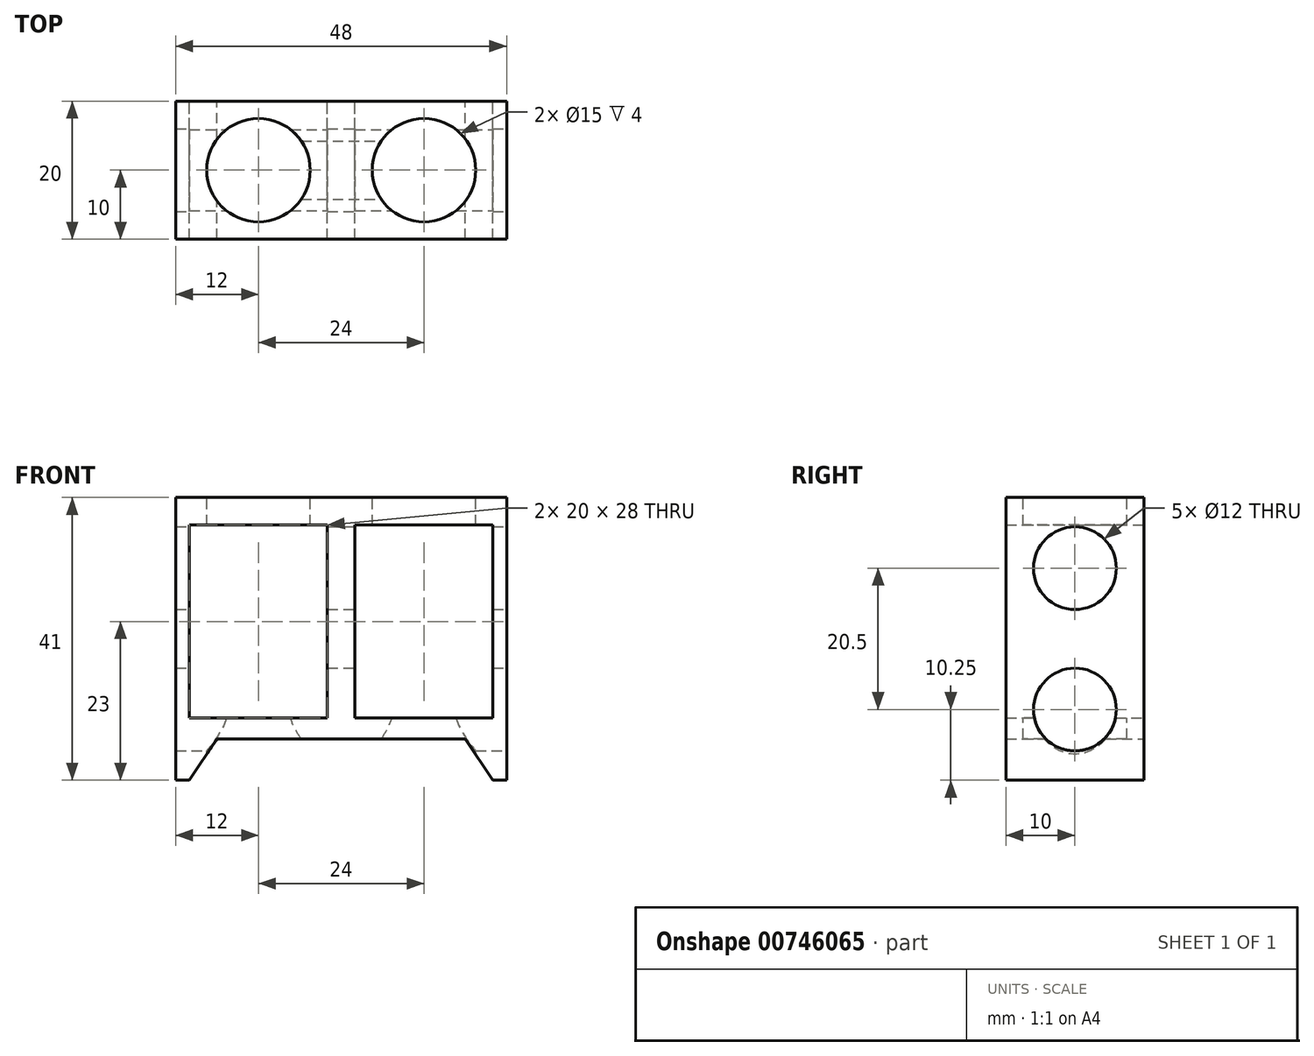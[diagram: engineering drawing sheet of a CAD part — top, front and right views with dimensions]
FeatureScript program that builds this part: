
annotation { "Feature Type Name" : "Feature", "Feature Type Description" : "" }
export const myFeature = defineFeature(function(context is Context, id is Id, definition is map)
    precondition{}
    {
        {
            var Q0;
            Q0=qCreatedBy(makeId("Front.planeOp"),FACE);
            var sketch = newSketch(context, id + "F0", { "sketchPlane" : qUnion([Q0])});
            skLineSegment(sketch, "E0", {"start": v(0, 0) * mm, "end": v(0, 45.25) * mm});
            skLineSegment(sketch, "E1", {"start": v(0, 0) * mm, "end": v(18, 0) * mm});
            skLineSegment(sketch, "E2", {"start": v(22, -6) * mm, "end": v(18, 0) * mm});
            skLineSegment(sketch, "E3", {"start": v(22, 35) * mm, "end": v(0, 35) * mm});
            skLineSegment(sketch, "E4", {"start": v(22, -6) * mm, "end": v(24, -6) * mm});
            skLineSegment(sketch, "E5", {"start": v(24, -6) * mm, "end": v(24, 35) * mm});
            skLineSegment(sketch, "E6", {"start": v(24, 35) * mm, "end": v(22, 35) * mm});
            skLineSegment(sketch, "E7", {"start": v(0, 0) * mm, "end": v(0, 3) * mm});
            skLineSegment(sketch, "E8", {"start": v(0, 3) * mm, "end": v(22, 3) * mm});
            skLineSegment(sketch, "E9", {"start": v(0, 3) * mm, "end": v(2, 3) * mm});
            skLineSegment(sketch, "E10", {"start": v(2, 3) * mm, "end": v(2, 31) * mm});
            skLineSegment(sketch, "E11", {"start": v(2, 31) * mm, "end": v(22, 31) * mm});
            skLineSegment(sketch, "E12", {"start": v(22, 31) * mm, "end": v(22, 3) * mm});
            skLineSegment(sketch, "E13.MirrorCS", {"start": v(-22, 35) * mm, "end": v(0, 35) * mm});
            skLineSegment(sketch, "E14.MirrorCS", {"start": v(-24, 35) * mm, "end": v(-22, 35) * mm});
            skLineSegment(sketch, "E15.MirrorCS", {"start": v(-24, -6) * mm, "end": v(-24, 35) * mm});
            skLineSegment(sketch, "E16.MirrorCS", {"start": v(-22, -6) * mm, "end": v(-18, 0) * mm});
            skLineSegment(sketch, "E17.MirrorCS", {"start": v(0, 0) * mm, "end": v(-18, 0) * mm});
            skLineSegment(sketch, "E18.MirrorCS", {"start": v(-22, -6) * mm, "end": v(-24, -6) * mm});
            skLineSegment(sketch, "E19.MirrorCS", {"start": v(0, 3) * mm, "end": v(-22, 3) * mm});
            skLineSegment(sketch, "E20.MirrorCS", {"start": v(-2, 3) * mm, "end": v(-2, 31) * mm});
            skLineSegment(sketch, "E21.MirrorCS", {"start": v(-22, 31) * mm, "end": v(-22, 3) * mm});
            skLineSegment(sketch, "E22.MirrorCS", {"start": v(-2, 31) * mm, "end": v(-22, 31) * mm});
            skSolve(sketch);
        }
        {
            var Q0;
            {var subQ6=sQuery(id+"F0.wireOp",EDGE,"E1");Q0=makeQuery(id+"F0.imprint","IMPRINT",FACE,{"disambiguationData":[TD([[makeQuery(id+"F0.imprint","IMPRINT",EDGE,{"derivedFrom":subQ6}),1.0]])]});}
            var Q1;
            {var subQ6=sQuery(id+"F0.wireOp",EDGE,"E13.MirrorCS");Q1=makeQuery(id+"F0.imprint","IMPRINT",FACE,{"disambiguationData":[TD([[makeQuery(id+"F0.imprint","IMPRINT",EDGE,{"derivedFrom":subQ6}),-1.0]])]});}
            extrude(context, id + "F1", {"entities" : qUnion([Q0, Q1]), "depth" : 20 * mm, "offsetDistance" : 25 * mm});
        }
        {
            var Q0;
            Q0=makeQuery(id+"F1.opExtrude","SWEPT_FACE",FACE,{"disambiguationData":[OSD([sQuery(id+"F0.wireOp",EDGE,"E3"),sQuery(id+"F0.wireOp",EDGE,"E6"),sQuery(id+"F0.wireOp",EDGE,"E13.MirrorCS"),sQuery(id+"F0.wireOp",EDGE,"E14.MirrorCS")])]});
            var sketch = newSketch(context, id + "F2", { "sketchPlane" : qUnion([Q0])});
            skLineSegment(sketch, "E23", {"start": v(-24, -10) * mm, "end": v(0, -10) * mm});
            skLineSegment(sketch, "E24", {"start": v(0, -10) * mm, "end": v(24, -10) * mm});
            skCircle(sketch, "E25", {"center": v(-12, -10) * mm, "radius": 7.5 * mm});
            skCircle(sketch, "E26", {"center": v(12, -10) * mm, "radius": 7.5 * mm});
            skSolve(sketch);
        }
        {
            var Q0;
            {var subQ0=sQuery(id+"F2.wireOp",EDGE,"E25");var subQ1=sQuery(id+"F2.wireOp",EDGE,"E23");var subQ2=makeQuery(id+"F2.imprint","INTERSECT",VERTEX,{"disambiguationData":[OD(0.0)],"derivedFrom":[subQ1,subQ0]});Q0=makeQuery(id+"F2.imprint","IMPRINT",FACE,{"disambiguationData":[TD([[makeQuery(id+"F2.imprint","IMPRINT",EDGE,{"disambiguationData":[TD([[subQ2,-1.0]])],"derivedFrom":subQ1}),-1.0]])]});}
            var Q1;
            {var subQ0=sQuery(id+"F2.wireOp",EDGE,"E25");var subQ1=sQuery(id+"F2.wireOp",EDGE,"E23");var subQ2=makeQuery(id+"F2.imprint","INTERSECT",VERTEX,{"disambiguationData":[OD(0.0)],"derivedFrom":[subQ1,subQ0]});Q1=makeQuery(id+"F2.imprint","IMPRINT",FACE,{"disambiguationData":[TD([[makeQuery(id+"F2.imprint","IMPRINT",EDGE,{"disambiguationData":[TD([[subQ2,-1.0]])],"derivedFrom":subQ1}),1.0]])]});}
            var Q2;
            {var subQ0=sQuery(id+"F2.wireOp",EDGE,"E26");var subQ1=sQuery(id+"F2.wireOp",EDGE,"E24");var subQ2=makeQuery(id+"F2.imprint","INTERSECT",VERTEX,{"disambiguationData":[OD(0.0)],"derivedFrom":[subQ1,subQ0]});Q2=makeQuery(id+"F2.imprint","IMPRINT",FACE,{"disambiguationData":[TD([[makeQuery(id+"F2.imprint","IMPRINT",EDGE,{"disambiguationData":[TD([[subQ2,-1.0]])],"derivedFrom":subQ1}),-1.0]])]});}
            var Q3;
            {var subQ0=sQuery(id+"F2.wireOp",EDGE,"E26");var subQ1=sQuery(id+"F2.wireOp",EDGE,"E24");var subQ2=makeQuery(id+"F2.imprint","INTERSECT",VERTEX,{"disambiguationData":[OD(0.0)],"derivedFrom":[subQ1,subQ0]});Q3=makeQuery(id+"F2.imprint","IMPRINT",FACE,{"disambiguationData":[TD([[makeQuery(id+"F2.imprint","IMPRINT",EDGE,{"disambiguationData":[TD([[subQ2,-1.0]])],"derivedFrom":subQ1}),1.0]])]});}
            extrude(context, id + "F3", {"entities" : qUnion([Q0, Q1, Q2, Q3]), "operationType" : NewBodyOperationType.REMOVE, "oppositeDirection" : true, "depth" : 50 * mm, "offsetDistance" : 25 * mm});
        }
        {
            var Q0;
            Q0=makeQuery(id+"F1.opExtrude","SWEPT_FACE",FACE,{"disambiguationData":[OSD([sQuery(id+"F0.wireOp",EDGE,"E5")])]});
            var sketch = newSketch(context, id + "F4", { "sketchPlane" : qUnion([Q0])});
            skLineSegment(sketch, "E27.0.0", {"start": v(0, -6) * mm, "end": v(0, 35) * mm});
            skLineSegment(sketch, "E27.0.1", {"start": v(0, 35) * mm, "end": v(-20, 35) * mm});
            skLineSegment(sketch, "E27.0.2", {"start": v(-20, 35) * mm, "end": v(-20, -6) * mm});
            skLineSegment(sketch, "E27.0.3", {"start": v(-20, -6) * mm, "end": v(0, -6) * mm});
            skLineSegment(sketch, "E28", {"start": v(-20, 14.5) * mm, "end": v(0, 14.5) * mm});
            skLineSegment(sketch, "E29", {"start": v(-10, 35) * mm, "end": v(-10, 14.5) * mm});
            skLineSegment(sketch, "E30", {"start": v(-10, 14.5) * mm, "end": v(-10, -6) * mm});
            skCircle(sketch, "E31", {"center": v(-10, 24.75) * mm, "radius": 6 * mm});
            skCircle(sketch, "E32", {"center": v(-10, 4.25) * mm, "radius": 6 * mm});
            skSolve(sketch);
        }
        {
            var Q0;
            {var subQ0=sQuery(id+"F4.wireOp",EDGE,"E31");var subQ1=sQuery(id+"F4.wireOp",EDGE,"E29");var subQ2=makeQuery(id+"F4.imprint","INTERSECT",VERTEX,{"disambiguationData":[OD(0.0)],"derivedFrom":[subQ1,subQ0]});Q0=makeQuery(id+"F4.imprint","IMPRINT",FACE,{"disambiguationData":[TD([[makeQuery(id+"F4.imprint","IMPRINT",EDGE,{"disambiguationData":[TD([[subQ2,-1.0]])],"derivedFrom":subQ1}),-1.0]])]});}
            var Q1;
            {var subQ0=sQuery(id+"F4.wireOp",EDGE,"E31");var subQ1=sQuery(id+"F4.wireOp",EDGE,"E29");var subQ2=makeQuery(id+"F4.imprint","INTERSECT",VERTEX,{"disambiguationData":[OD(0.0)],"derivedFrom":[subQ1,subQ0]});Q1=makeQuery(id+"F4.imprint","IMPRINT",FACE,{"disambiguationData":[TD([[makeQuery(id+"F4.imprint","IMPRINT",EDGE,{"disambiguationData":[TD([[subQ2,-1.0]])],"derivedFrom":subQ1}),1.0]])]});}
            var Q2;
            {var subQ0=sQuery(id+"F4.wireOp",EDGE,"E32");var subQ1=sQuery(id+"F4.wireOp",EDGE,"E30");var subQ2=makeQuery(id+"F4.imprint","INTERSECT",VERTEX,{"disambiguationData":[OD(0.0)],"derivedFrom":[subQ1,subQ0]});Q2=makeQuery(id+"F4.imprint","IMPRINT",FACE,{"disambiguationData":[TD([[makeQuery(id+"F4.imprint","IMPRINT",EDGE,{"disambiguationData":[TD([[subQ2,-1.0]])],"derivedFrom":subQ1}),1.0]])]});}
            var Q3;
            {var subQ0=sQuery(id+"F4.wireOp",EDGE,"E32");var subQ1=sQuery(id+"F4.wireOp",EDGE,"E30");var subQ2=makeQuery(id+"F4.imprint","INTERSECT",VERTEX,{"disambiguationData":[OD(0.0)],"derivedFrom":[subQ1,subQ0]});Q3=makeQuery(id+"F4.imprint","IMPRINT",FACE,{"disambiguationData":[TD([[makeQuery(id+"F4.imprint","IMPRINT",EDGE,{"disambiguationData":[TD([[subQ2,-1.0]])],"derivedFrom":subQ1}),-1.0]])]});}
            extrude(context, id + "F5", {"entities" : qUnion([Q0, Q1, Q2, Q3]), "operationType" : NewBodyOperationType.REMOVE, "oppositeDirection" : true, "depth" : 50 * mm, "offsetDistance" : 25 * mm});
        }
    });
